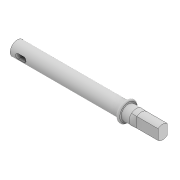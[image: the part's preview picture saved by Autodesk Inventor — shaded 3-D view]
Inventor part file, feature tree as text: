
AUTODESK INVENTOR PART (.ipt)
format: ipt  version: 2022 (Build 260153000, 153)  size: 158,720 bytes
history: native  units: mm
features: extrude x5, sketch x5, plane x2, fillet x2, other x2, projected_geometry x2, thicken_offset x1, loft x1, chamfer x1
ambient origin geometry x8: Origin, YZ Plane, XZ Plane, XY Plane, X Axis, Y Axis, Z Axis, Center Point
bodies: Solid1 (feature_tree)
feature tree (21):
  extrude  "Extrusion1"  Depth=2.35mm TaperAngle=0.0deg
  extrude  "Extrusion2"  Depth=2.0mm
  plane  "Work Plane1"
  extrude  "Extrusion3"  Depth=1.0mm
  thicken_offset  "Thicken2"
  loft  "Loft1"
  plane  "Work Plane2"
  extrude  "Extrusion4"  Depth=0.5mm
  fillet  "Fillet1"  Radius=2.0mm
  extrude  "Offset"  TaperAngle=0.0deg  [1 undecoded]
  fillet  "Fillet2"  [1 undecoded]
  chamfer  "Chamfer1"  [1 undecoded]
  sketch  "Sketch1"  dims[d2=0.0mm d9=2.35mm d10=0.0mm]
  sketch  "Sketch2"  dims[d17=1.8mm d20=2.0mm]
  sketch  "Sketch3"  dims[d21=1.0mm d22=7.0mm]
  other  "Edges1"
  other  "Edges2"
  sketch  "Sketch4"  dims[d23=5.5mm d24=4.0mm]
  sketch  "Sketch5"  dims[d25=8.0mm d26=0.0mm d27=0.15mm d28=0.1mm d29=2.0mm d30=0.0mm d31=90.0deg d32=0.0mm d33=90.0deg d34=-41.0mm d35=7.5mm d36=1.0mm d37=0.0mm d38=0.5mm d42=9.0mm d43=0.0mm d44=0.5mm d45=0.5mm d46=2.0mm d47=45.0deg d48=5.3mm]
  projected_geometry  "Project Cut Edges1"
  projected_geometry  "Project Cut Edges2"
note: 3 required parameter values undecoded (feature->parameter linkage not recoverable at this tier; creation-order binding heuristic only, values carry confidence <= 0.55)
